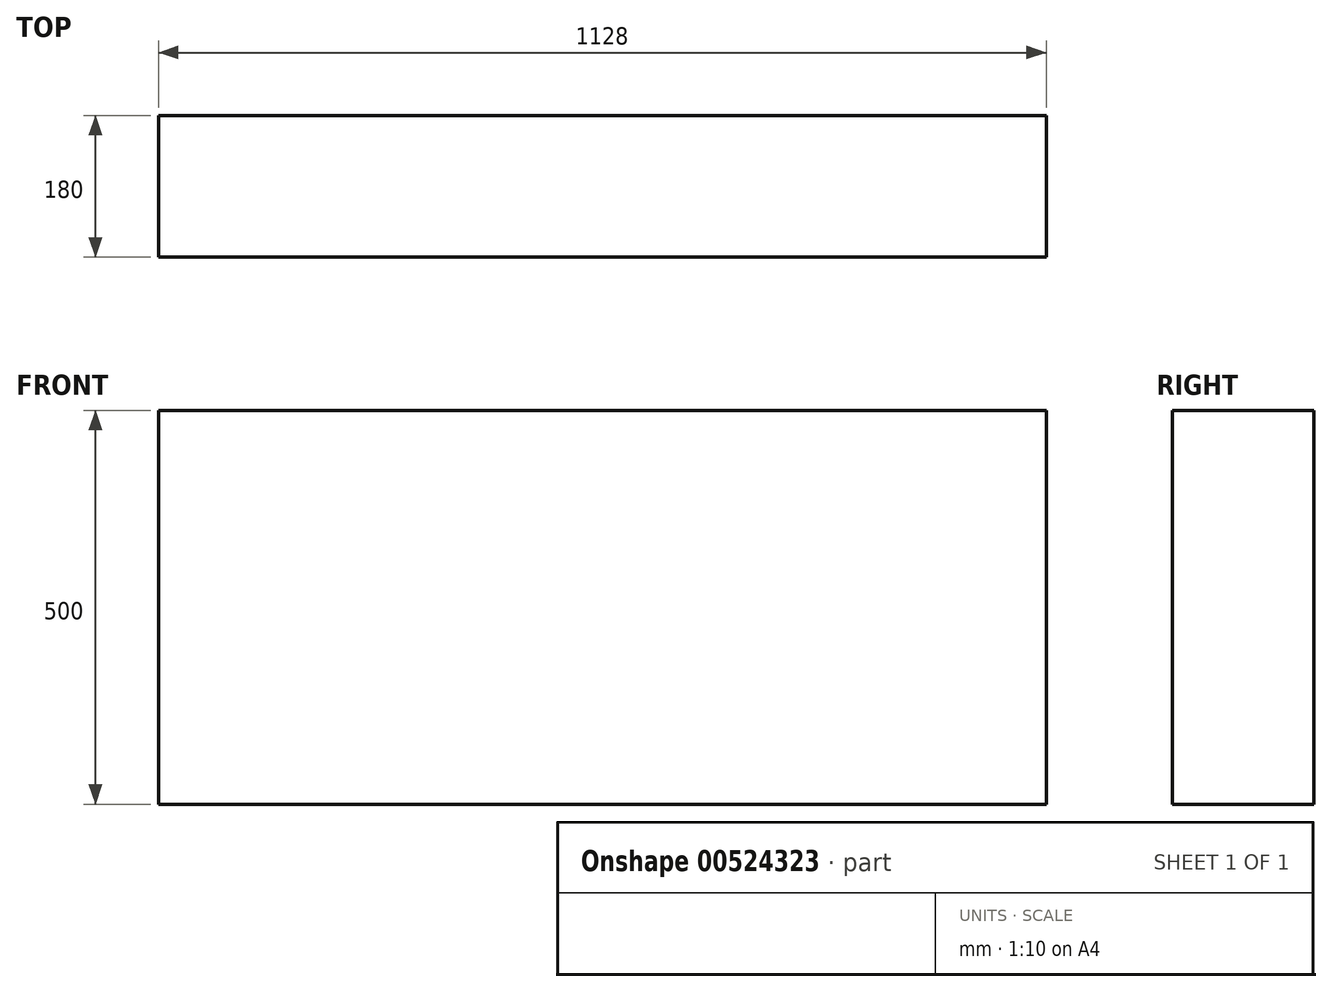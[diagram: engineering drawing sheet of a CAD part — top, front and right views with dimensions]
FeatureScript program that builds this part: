
annotation { "Feature Type Name" : "Feature", "Feature Type Description" : "" }
export const myFeature = defineFeature(function(context is Context, id is Id, definition is map)
    precondition{}
    {
        {
            var Q0;
            Q0=qCreatedBy(makeId("Top.planeOp"),FACE);
            var sketch = newSketch(context, id + "F0", { "sketchPlane" : qUnion([Q0])});
            skLineSegment(sketch, "E0.bottom", {"start": v(564, -90) * mm, "end": v(-564, -90) * mm});
            skLineSegment(sketch, "E0.top", {"start": v(564, 90) * mm, "end": v(-564, 90) * mm});
            skLineSegment(sketch, "E0.left", {"start": v(564, -90) * mm, "end": v(564, 90) * mm});
            skLineSegment(sketch, "E0.right", {"start": v(-564, -90) * mm, "end": v(-564, 90) * mm});
            skPoint(sketch, "E0.middle", {"position": v(0, 0) * mm});
            skSolve(sketch);
        }
        {
            var Q0;
            Q0 = qSketchRegion(id + "F0", true);
            extrude(context, id + "F1", {"entities" : qUnion([Q0]), "depth" : 500 * mm, "offsetDistance" : 25 * mm});
        }
    });
